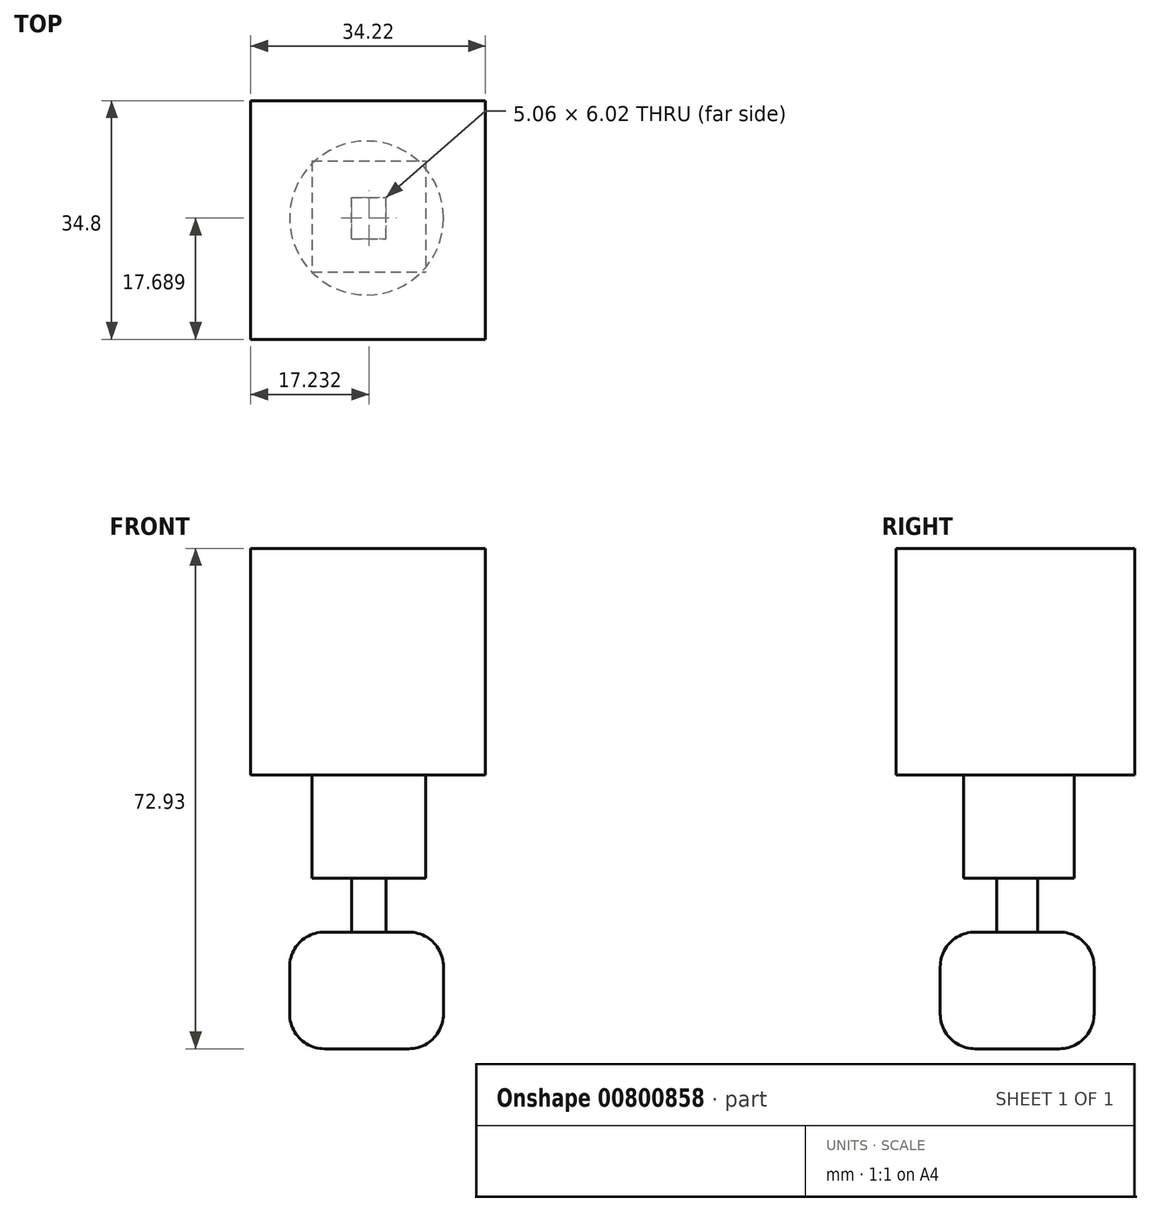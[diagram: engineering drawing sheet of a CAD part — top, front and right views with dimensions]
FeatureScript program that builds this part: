
annotation { "Feature Type Name" : "Feature", "Feature Type Description" : "" }
export const myFeature = defineFeature(function(context is Context, id is Id, definition is map)
    precondition{}
    {
        {
            var Q0;
            Q0=qCreatedBy(makeId("Front.planeOp"),FACE);
            var sketch = newSketch(context, id + "F0", { "sketchPlane" : qUnion([Q0])});
            skLineSegment(sketch, "E0.bottom", {"start": v(-11.59, 16.03) * mm, "end": v(22.63, 16.03) * mm});
            skLineSegment(sketch, "E0.top", {"start": v(-11.59, -17) * mm, "end": v(22.63, -17) * mm});
            skLineSegment(sketch, "E0.left", {"start": v(-11.59, 16.03) * mm, "end": v(-11.59, -17) * mm});
            skLineSegment(sketch, "E0.right", {"start": v(22.63, 16.03) * mm, "end": v(22.63, -17) * mm});
            skSolve(sketch);
        }
        {
            var Q0;
            Q0=makeQuery(id+"F0.imprint","IMPRINT",FACE,{"disambiguationData":[TD([[makeQuery(id+"F0.imprint","IMPRINT",EDGE,{"derivedFrom":sQuery(id+"F0.wireOp",EDGE,"E0.bottom")}),-1.0]])]});
            extrude(context, id + "F1", {"entities" : qUnion([Q0]), "depth" : 34.8 * mm, "offsetDistance" : 25.4 * mm});
        }
        {
            var Q0;
            Q0=qCreatedBy(makeId("Top.planeOp"),FACE);
            var sketch = newSketch(context, id + "F2", { "sketchPlane" : qUnion([Q0])});
            skLineSegment(sketch, "E1.bottom", {"start": v(-2.67, -8.8) * mm, "end": v(13.96, -8.8) * mm});
            skLineSegment(sketch, "E1.top", {"start": v(-2.67, -24.94) * mm, "end": v(13.96, -24.94) * mm});
            skLineSegment(sketch, "E1.left", {"start": v(-2.67, -8.8) * mm, "end": v(-2.67, -24.94) * mm});
            skLineSegment(sketch, "E1.right", {"start": v(13.96, -8.8) * mm, "end": v(13.96, -24.94) * mm});
            skSolve(sketch);
        }
        {
            var Q0;
            Q0 = qSketchRegion(id + "F2", true);
            extrude(context, id + "F3", {"entities" : qUnion([Q0]), "operationType" : NewBodyOperationType.ADD, "oppositeDirection" : true, "depth" : 32 * mm, "offsetDistance" : 25.4 * mm});
        }
        {
            var Q0;
            Q0=qCreatedBy(makeId("Top.planeOp"),FACE);
            var sketch = newSketch(context, id + "F4", { "sketchPlane" : qUnion([Q0])});
            skLineSegment(sketch, "E2.bottom", {"start": v(3.11, -20.12) * mm, "end": v(8.17, -20.12) * mm});
            skLineSegment(sketch, "E2.top", {"start": v(3.11, -14.1) * mm, "end": v(8.17, -14.1) * mm});
            skLineSegment(sketch, "E2.left", {"start": v(3.11, -20.12) * mm, "end": v(3.11, -14.1) * mm});
            skLineSegment(sketch, "E2.right", {"start": v(8.17, -20.12) * mm, "end": v(8.17, -14.1) * mm});
            skSolve(sketch);
        }
        {
            var Q0;
            Q0 = qSketchRegion(id + "F4", true);
            extrude(context, id + "F5", {"entities" : qUnion([Q0]), "operationType" : NewBodyOperationType.ADD, "oppositeDirection" : true, "depth" : 39.88 * mm, "offsetDistance" : 25.4 * mm});
        }
        {
            var Q0;
            Q0=makeQuery(id+"F5.opExtrude","CAP_FACE",FACE,{"disambiguationData":[OSD([sQuery(id+"F4.wireOp",EDGE,"E2.bottom"),sQuery(id+"F4.wireOp",EDGE,"E2.top"),sQuery(id+"F4.wireOp",EDGE,"E2.left"),sQuery(id+"F4.wireOp",EDGE,"E2.right")])],"isStart":false});
            var sketch = newSketch(context, id + "F6", { "sketchPlane" : qUnion([Q0])});
            skCircle(sketch, "E3", {"center": v(5.3, 17.11) * mm, "radius": 11.22 * mm});
            skPoint(sketch, "E3.centerSnap0", {"position": v(8.17, 17.11) * mm});
            skSolve(sketch);
        }
        {
            var Q0;
            Q0 = qSketchRegion(id + "F6", true);
            extrude(context, id + "F7", {"entities" : qUnion([Q0]), "operationType" : NewBodyOperationType.ADD, "depth" : 17.02 * mm, "offsetDistance" : 25.4 * mm});
        }
        {
            var Q0;
            Q0=makeQuery(id+"F7.opExtrude","CAP_EDGE",EDGE,{"disambiguationData":[OSD([sQuery(id+"F6.wireOp",EDGE,"E3")])],"isStart":false});
            var Q1;
            Q1=makeQuery(id+"F7.opExtrude","CAP_EDGE",EDGE,{"disambiguationData":[OSD([sQuery(id+"F6.wireOp",EDGE,"E3")])],"isStart":true});
            fillet(context, id + "F8", {"entities" : qUnion([Q0, Q1]), "radius" : 5.08 * mm, "tangentPropagation" : true, "allowEdgeOverflow" : false});
        }
    });
